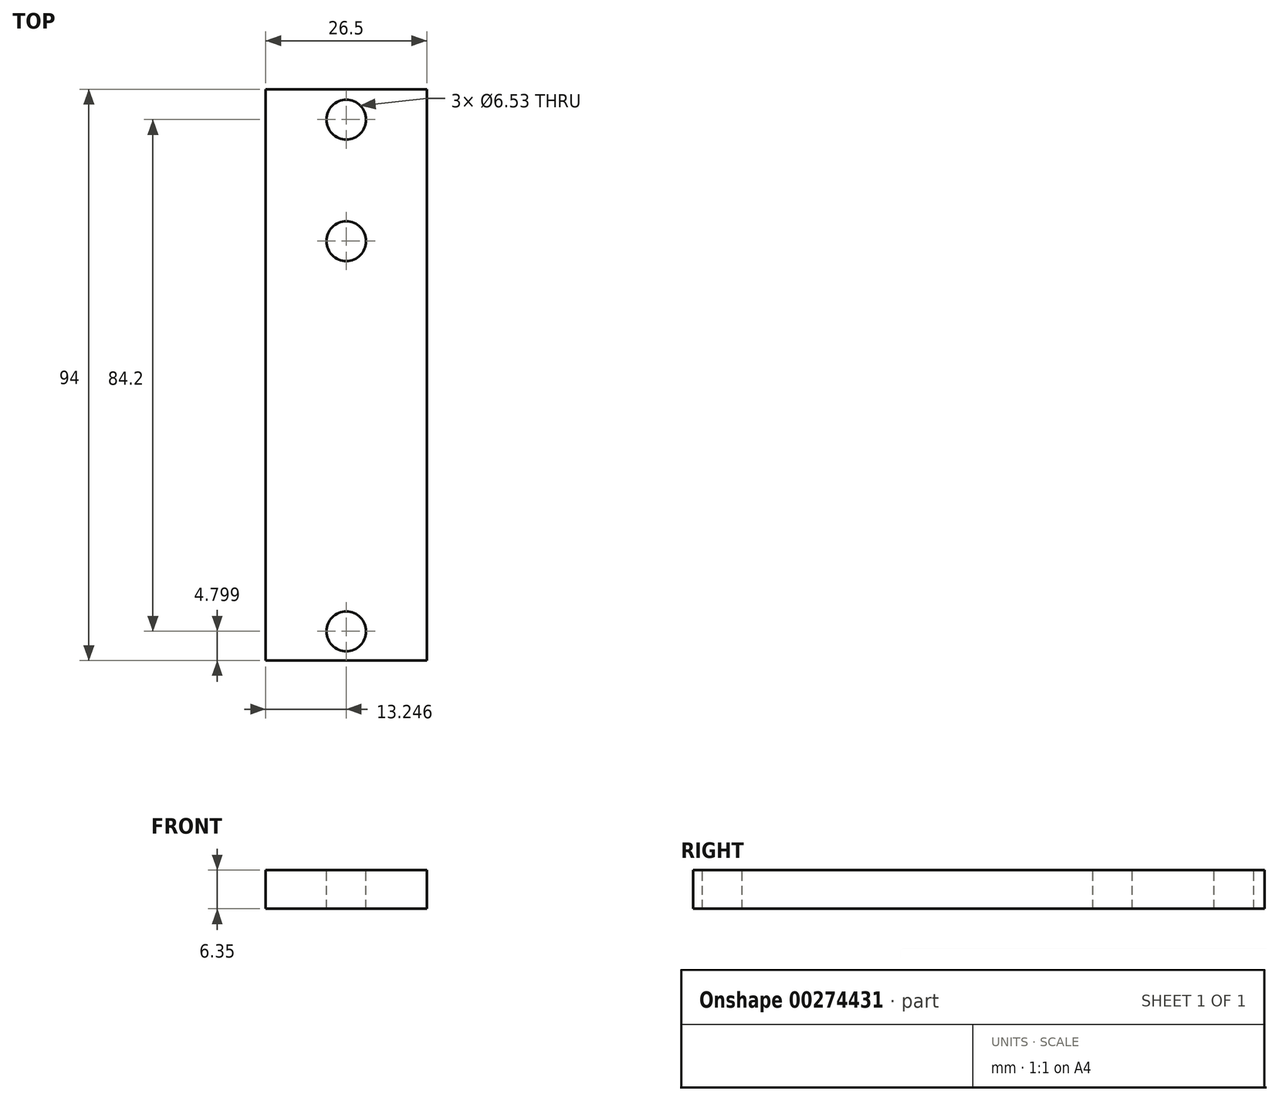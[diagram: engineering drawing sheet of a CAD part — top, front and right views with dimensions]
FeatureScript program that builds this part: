
annotation { "Feature Type Name" : "Feature", "Feature Type Description" : "" }
export const myFeature = defineFeature(function(context is Context, id is Id, definition is map)
    precondition{}
    {
        {
            var Q0;
            Q0=qCreatedBy(makeId("Top.planeOp"),FACE);
            var sketch = newSketch(context, id + "F0", { "sketchPlane" : qUnion([Q0])});
            skLineSegment(sketch, "E0.bottom", {"start": v(-13.13, 66.53) * mm, "end": v(13.37, 66.53) * mm});
            skLineSegment(sketch, "E0.top", {"start": v(-13.13, -27.47) * mm, "end": v(13.37, -27.47) * mm});
            skLineSegment(sketch, "E0.left", {"start": v(-13.13, 66.53) * mm, "end": v(-13.13, -27.47) * mm});
            skLineSegment(sketch, "E0.right", {"start": v(13.37, 66.53) * mm, "end": v(13.37, -27.47) * mm});
            skSolve(sketch);
        }
        {
            var Q0;
            Q0=makeQuery(id+"F0.imprint","IMPRINT",FACE,{"disambiguationData":[TD([[makeQuery(id+"F0.imprint","IMPRINT",EDGE,{"derivedFrom":sQuery(id+"F0.wireOp",EDGE,"E0.bottom")}),-1.0]])]});
            extrude(context, id + "F1", {"entities" : qUnion([Q0]), "depth" : 6.35 * mm});
        }
        {
            var Q0;
            Q0=makeQuery(id+"F1.opExtrude","CAP_FACE",FACE,{"disambiguationData":[OSD([sQuery(id+"F0.wireOp",EDGE,"E0.bottom"),sQuery(id+"F0.wireOp",EDGE,"E0.top"),sQuery(id+"F0.wireOp",EDGE,"E0.left"),sQuery(id+"F0.wireOp",EDGE,"E0.right")])],"isStart":false});
            var sketch = newSketch(context, id + "F2", { "sketchPlane" : qUnion([Q0])});
            skPoint(sketch, "E1", {"position": v(0.12, 61.53) * mm});
            skPoint(sketch, "E2", {"position": v(0.12, 41.53) * mm});
            skPoint(sketch, "E3", {"position": v(0.12, -22.67) * mm});
            skSolve(sketch);
        }
        {
            var Q0;
            Q0=sQuery(id+"F2.wireOp",VERTEX,"E1");
            var Q1;
            Q1=sQuery(id+"F2.wireOp",VERTEX,"E2");
            var Q2;
            Q2=sQuery(id+"F2.wireOp",VERTEX,"E3");
            var Q3;
            Q3=makeQuery(id+"F1.opExtrude","SWEPT_BODY",BODY,{"disambiguationData":[OSD([sQuery(id+"F0.wireOp",EDGE,"E0.bottom"),sQuery(id+"F0.wireOp",EDGE,"E0.top"),sQuery(id+"F0.wireOp",EDGE,"E0.left"),sQuery(id+"F0.wireOp",EDGE,"E0.right")])]});
            hole(context, id + "F3", {"style" : HoleStyle.SIMPLE, "endStyle" : HoleEndStyle.THROUGH, "holeDiameter" : 6.53 * mm, "tappedDepth" : 12 * mm, "tapClearance" : 3, "locations" : qUnion([Q0, Q1, Q2]), "scope" : qUnion([Q3])});
        }
    });
